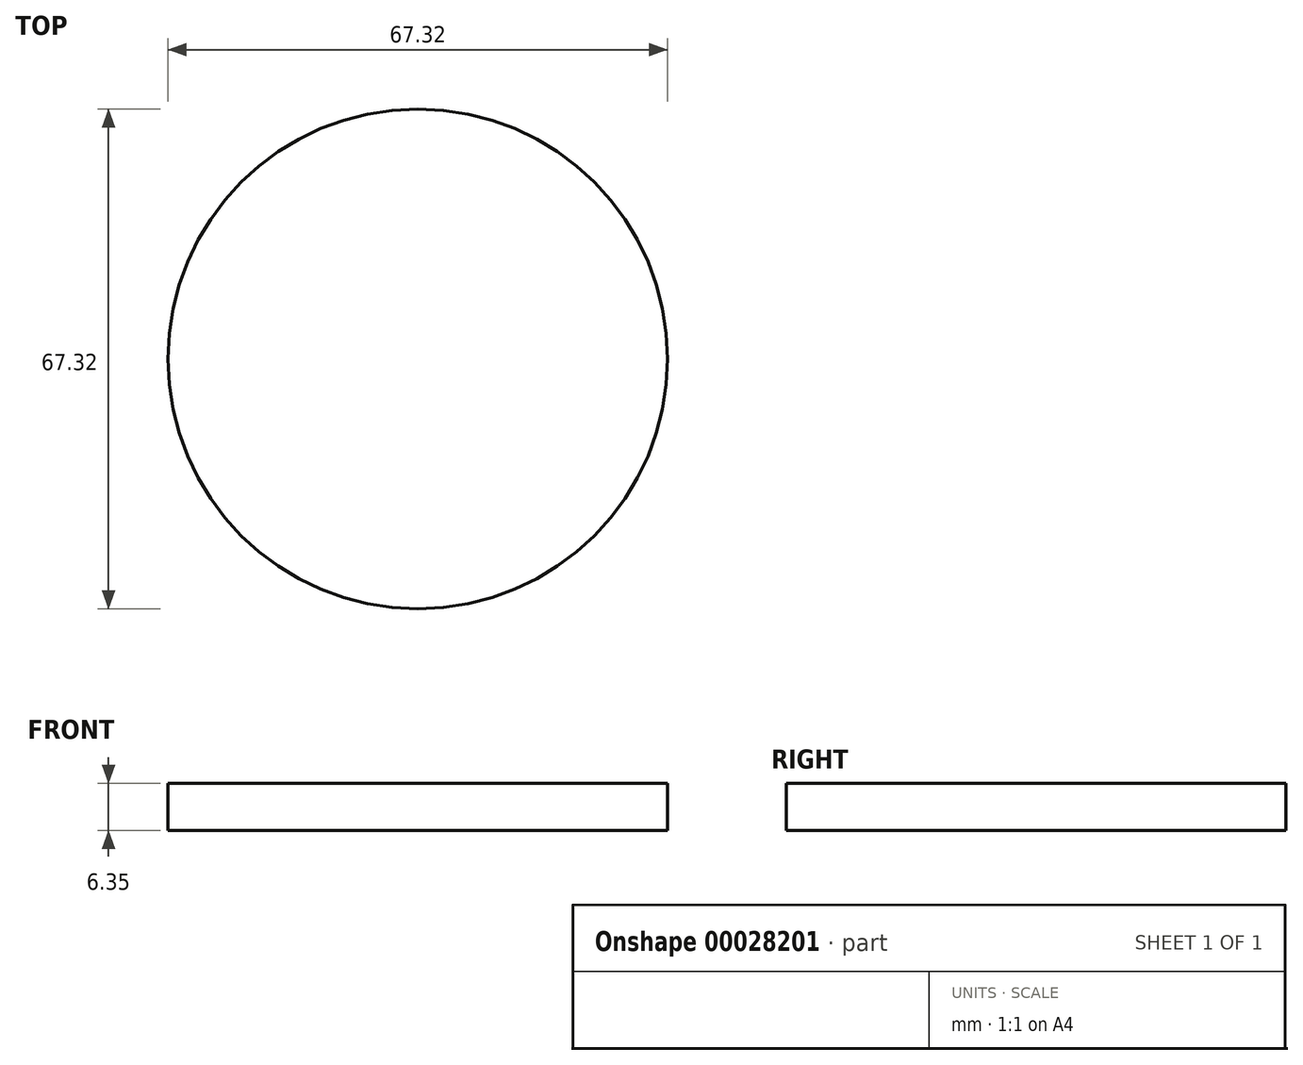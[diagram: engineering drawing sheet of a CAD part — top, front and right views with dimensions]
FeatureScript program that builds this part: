
annotation { "Feature Type Name" : "Feature", "Feature Type Description" : "" }
export const myFeature = defineFeature(function(context is Context, id is Id, definition is map)
    precondition{}
    {
        {
            var Q0;
            Q0=qCreatedBy(makeId("Top.planeOp"),FACE);
            var sketch = newSketch(context, id + "F0", { "sketchPlane" : qUnion([Q0])});
            skCircle(sketch, "E0", {"center": v(0, 0) * mm, "radius": 33.66 * mm});
            skSolve(sketch);
        }
        {
            var Q0;
            Q0 = qSketchRegion(id + "F0", true);
            extrude(context, id + "F1", {"entities" : qUnion([Q0]), "depth" : 6.35 * mm});
        }
    });
